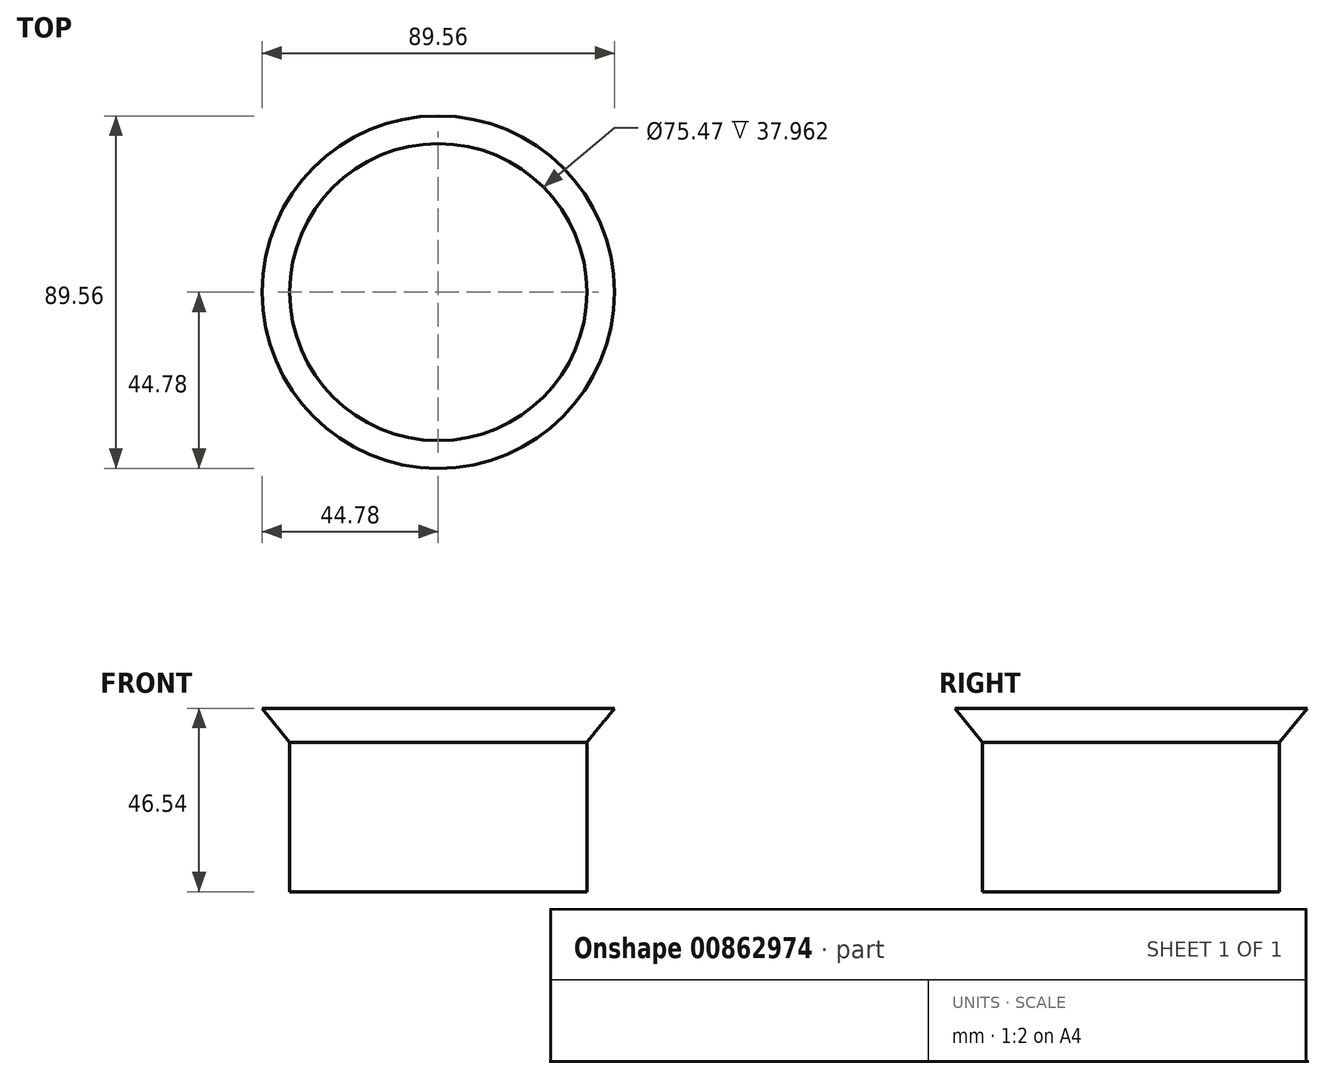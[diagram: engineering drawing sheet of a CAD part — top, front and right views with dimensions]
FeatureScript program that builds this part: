
annotation { "Feature Type Name" : "Feature", "Feature Type Description" : "" }
export const myFeature = defineFeature(function(context is Context, id is Id, definition is map)
    precondition{}
    {
        {
            var Q0;
            Q0=qCreatedBy(makeId("Front.planeOp"),FACE);
            var sketch = newSketch(context, id + "F0", { "sketchPlane" : qUnion([Q0])});
            skLineSegment(sketch, "E0", {"start": v(0, 0) * mm, "end": v(37.73, 0) * mm});
            skLineSegment(sketch, "E1", {"start": v(37.73, 0) * mm, "end": v(37.73, 37.96) * mm});
            skLineSegment(sketch, "E2", {"start": v(37.73, 37.96) * mm, "end": v(44.78, 46.54) * mm});
            skLineSegment(sketch, "E3", {"start": v(0, 0) * mm, "end": v(0, 61.69) * mm, "construction": true});
            skSolve(sketch);
        }
        {
            var Q0;
            Q0=sQuery(id+"F0.wireOp",EDGE,"E1");
            var Q1;
            Q1=sQuery(id+"F0.wireOp",EDGE,"E2");
            var Q2;
            Q2=sQuery(id+"F0.wireOp",EDGE,"E0");
            var Q3;
            Q3=sQuery(id+"F0.wireOp",EDGE,"E3");
            revolve(context, id + "F1", {"bodyType" : ToolBodyType.SURFACE, "surfaceOperationType" : NewSurfaceOperationType.NEW, "surfaceEntities" : qUnion([Q0, Q1, Q2]), "axis" : qUnion([Q3]), "revolveType" : RevolveType.FULL});
        }
    });
